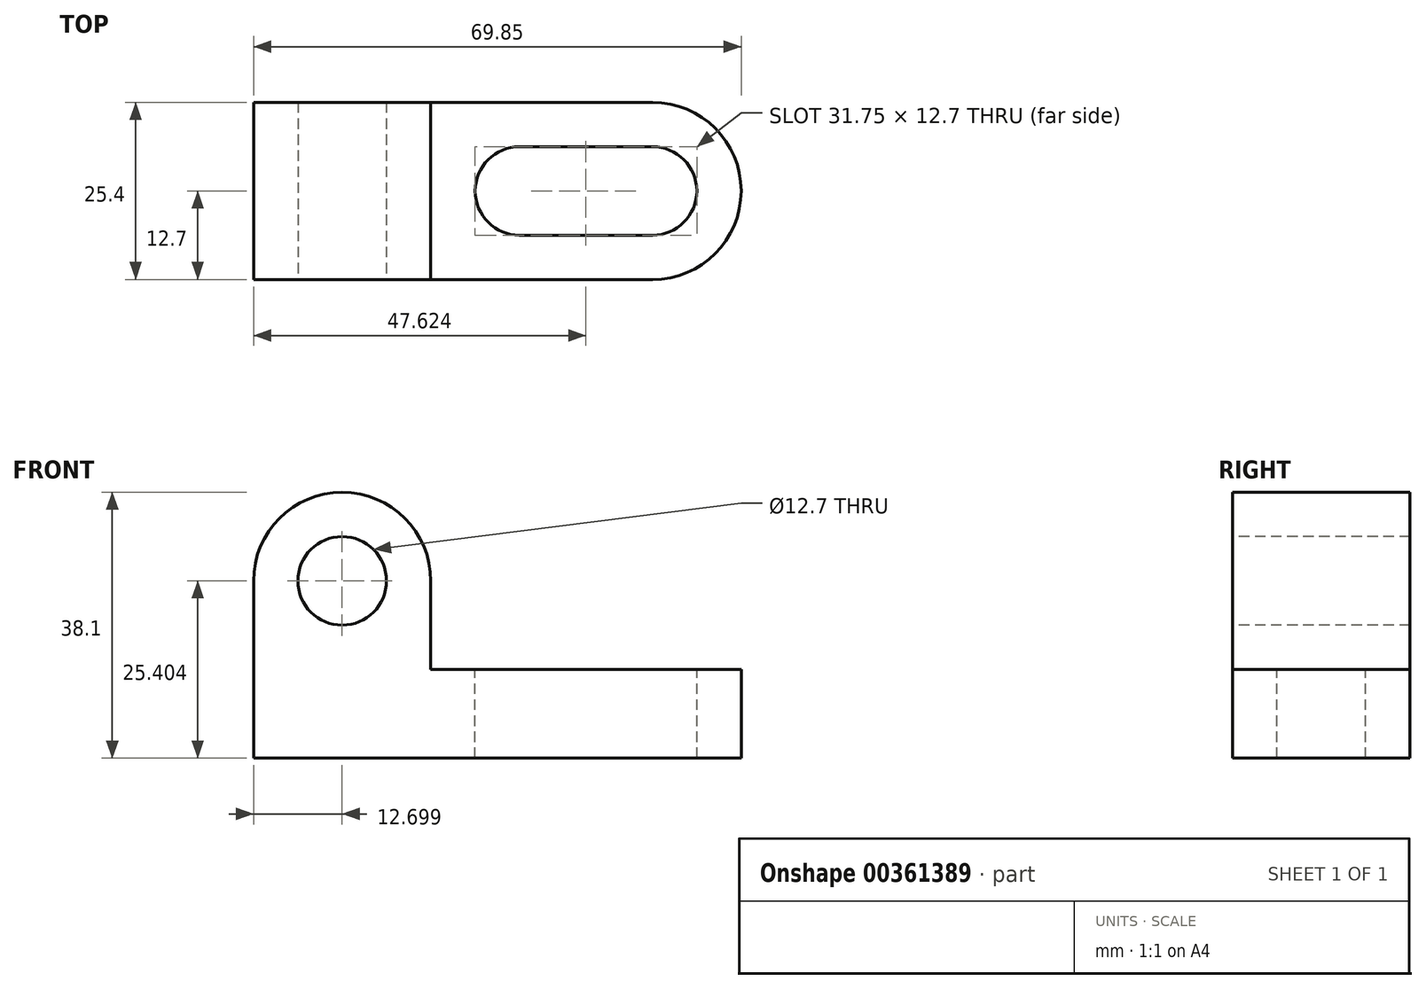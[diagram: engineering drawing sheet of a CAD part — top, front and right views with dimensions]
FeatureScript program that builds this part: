
annotation { "Feature Type Name" : "Feature", "Feature Type Description" : "" }
export const myFeature = defineFeature(function(context is Context, id is Id, definition is map)
    precondition{}
    {
        {
            var Q0;
            Q0=qCreatedBy(makeId("Front.planeOp"),FACE);
            var sketch = newSketch(context, id + "F0", { "sketchPlane" : qUnion([Q0])});
            skLineSegment(sketch, "E0", {"start": v(-44.44, 26.21) * mm, "end": v(-44.44, -11.89) * mm});
            skLineSegment(sketch, "E1", {"start": v(-44.44, -11.89) * mm, "end": v(25.4, -11.89) * mm});
            skLineSegment(sketch, "E2", {"start": v(25.4, -11.89) * mm, "end": v(25.4, 0.81) * mm});
            skLineSegment(sketch, "E3", {"start": v(-19.04, 0.81) * mm, "end": v(25.4, 0.81) * mm});
            skLineSegment(sketch, "E4", {"start": v(-19.04, 0.81) * mm, "end": v(-19.04, 26.21) * mm});
            skLineSegment(sketch, "E5", {"start": v(-19.04, 26.21) * mm, "end": v(-44.44, 26.21) * mm});
            skSolve(sketch);
        }
        {
            var Q0;
            Q0 = qSketchRegion(id + "F0", true);
            extrude(context, id + "F1", {"entities" : qUnion([Q0]), "depth" : 25.4 * mm});
        }
        {
            var Q0;
            Q0=makeQuery(id+"F1.opExtrude","CAP_FACE",FACE,{"disambiguationData":[OSD([sQuery(id+"F0.wireOp",EDGE,"E0"),sQuery(id+"F0.wireOp",EDGE,"E1"),sQuery(id+"F0.wireOp",EDGE,"E2"),sQuery(id+"F0.wireOp",EDGE,"E3"),sQuery(id+"F0.wireOp",EDGE,"E4"),sQuery(id+"F0.wireOp",EDGE,"E5")])],"isStart":false});
            var sketch = newSketch(context, id + "F2", { "sketchPlane" : qUnion([Q0])});
            skCircle(sketch, "E6", {"center": v(-31.74, 13.51) * mm, "radius": 6.35 * mm});
            skArc(sketch, "E7", {"start": v(-19.04, 13.51) * mm, "mid": v(-31.74, 26.21) * mm, "end": v(-44.44, 13.51) * mm});
            skSolve(sketch);
        }
        {
            var Q0;
            Q0 = qSketchRegion(id + "F2", true);
            var Q1;
            {var subQ0=sQuery(id+"F2.wireOp",EDGE,"E7");var subQ1=makeQuery(id+"F1.opExtrude","CAP_EDGE",EDGE,{"disambiguationData":[OSD([sQuery(id+"F0.wireOp",EDGE,"E0")])],"isStart":false});var subQ2=makeQuery(id+"F2.imprint","INTERSECT",VERTEX,{"derivedFrom":[subQ1,subQ0]});Q1=makeQuery(id+"F2.imprint","IMPRINT",FACE,{"disambiguationData":[TD([[makeQuery(id+"F2.imprint","IMPRINT",EDGE,{"disambiguationData":[TD([[subQ2,1.0]])],"derivedFrom":subQ0}),-1.0]])]});}
            var Q2;
            {var subQ0=sQuery(id+"F2.wireOp",EDGE,"E7");var subQ1=makeQuery(id+"F1.opExtrude","CAP_EDGE",EDGE,{"disambiguationData":[OSD([sQuery(id+"F0.wireOp",EDGE,"E4")])],"isStart":false});var subQ2=makeQuery(id+"F2.imprint","INTERSECT",VERTEX,{"derivedFrom":[subQ1,subQ0]});Q2=makeQuery(id+"F2.imprint","IMPRINT",FACE,{"disambiguationData":[TD([[makeQuery(id+"F2.imprint","IMPRINT",EDGE,{"disambiguationData":[TD([[subQ2,-1.0]])],"derivedFrom":subQ0}),-1.0]])]});}
            extrude(context, id + "F3", {"entities" : qUnion([Q0, Q1, Q2]), "operationType" : NewBodyOperationType.REMOVE, "oppositeDirection" : true, "depth" : 25.4 * mm});
        }
        {
            var Q0;
            Q0=makeQuery(id+"F1.opExtrude","SWEPT_FACE",FACE,{"disambiguationData":[OSD([sQuery(id+"F0.wireOp",EDGE,"E3")])]});
            var sketch = newSketch(context, id + "F4", { "sketchPlane" : qUnion([Q0])});
            skLineSegment(sketch, "E8", {"start": v(-19.04, 0) * mm, "end": v(12.7, 0) * mm});
            skLineSegment(sketch, "E9", {"start": v(25.4, -12.7) * mm, "end": v(25.4, -12.7) * mm});
            skLineSegment(sketch, "E10", {"start": v(12.7, -25.4) * mm, "end": v(-19.04, -25.4) * mm});
            skPoint(sketch, "E11.visualSharp", {"position": v(25.4, 0) * mm});
            skArc(sketch, "E11.filletArc", {"start": v(25.4, -12.7) * mm, "mid": v(21.69, -3.72) * mm, "end": v(12.7, 0) * mm});
            skPoint(sketch, "E12.visualSharp", {"position": v(25.4, -25.4) * mm});
            skArc(sketch, "E12.filletArc", {"start": v(12.7, -25.4) * mm, "mid": v(21.69, -21.68) * mm, "end": v(25.4, -12.7) * mm});
            skCircle(sketch, "E13", {"center": v(12.7, -12.7) * mm, "radius": 6.35 * mm});
            skCircle(sketch, "E14", {"center": v(-6.34, -12.7) * mm, "radius": 6.35 * mm});
            skPoint(sketch, "E14.centerSnap0", {"position": v(-19.04, -12.7) * mm});
            skLineSegment(sketch, "E15", {"start": v(-6.34, -6.35) * mm, "end": v(12.7, -6.35) * mm});
            skLineSegment(sketch, "E16", {"start": v(12.7, -6.35) * mm, "end": v(12.7, -19.05) * mm});
            skLineSegment(sketch, "E17", {"start": v(12.7, -19.05) * mm, "end": v(-6.34, -19.05) * mm});
            skSolve(sketch);
        }
        {
            var Q0;
            {var subQ0=sQuery(id+"F4.wireOp",EDGE,"E14");var subQ1=makeQuery(id+"F4.imprint","INTERSECT",VERTEX,{"derivedFrom":[subQ0,sQuery(id+"F4.wireOp",EDGE,"E15")]});Q0=makeQuery(id+"F4.imprint","IMPRINT",FACE,{"disambiguationData":[TD([[makeQuery(id+"F4.imprint","IMPRINT",EDGE,{"disambiguationData":[TD([[subQ1,-1.0]])],"derivedFrom":subQ0}),1.0]])]});}
            var Q1;
            {var subQ1=sQuery(id+"F4.wireOp",EDGE,"E15");Q1=makeQuery(id+"F4.imprint","IMPRINT",FACE,{"disambiguationData":[TD([[makeQuery(id+"F4.imprint","IMPRINT",EDGE,{"derivedFrom":subQ1}),-1.0]])]});}
            var Q2;
            {var subQ0=sQuery(id+"F4.wireOp",EDGE,"E16");Q2=makeQuery(id+"F4.imprint","IMPRINT",FACE,{"disambiguationData":[TD([[makeQuery(id+"F4.imprint","IMPRINT",EDGE,{"derivedFrom":subQ0}),1.0]])]});}
            var Q3;
            {var subQ0=sQuery(id+"F4.wireOp",EDGE,"E16");Q3=makeQuery(id+"F4.imprint","IMPRINT",FACE,{"disambiguationData":[TD([[makeQuery(id+"F4.imprint","IMPRINT",EDGE,{"derivedFrom":subQ0}),-1.0]])]});}
            var Q4;
            {var subQ0=sQuery(id+"F4.wireOp",EDGE,"E12.filletArc");Q4=makeQuery(id+"F4.imprint","IMPRINT",FACE,{"disambiguationData":[TD([[makeQuery(id+"F4.imprint","IMPRINT",EDGE,{"derivedFrom":subQ0}),-1.0]])]});}
            var Q5;
            {var subQ0=sQuery(id+"F4.wireOp",EDGE,"E11.filletArc");Q5=makeQuery(id+"F4.imprint","IMPRINT",FACE,{"disambiguationData":[TD([[makeQuery(id+"F4.imprint","IMPRINT",EDGE,{"derivedFrom":subQ0}),-1.0]])]});}
            extrude(context, id + "F5", {"entities" : qUnion([Q0, Q1, Q2, Q3, Q4, Q5]), "operationType" : NewBodyOperationType.REMOVE, "oppositeDirection" : true, "depth" : 25.4 * mm});
        }
    });
